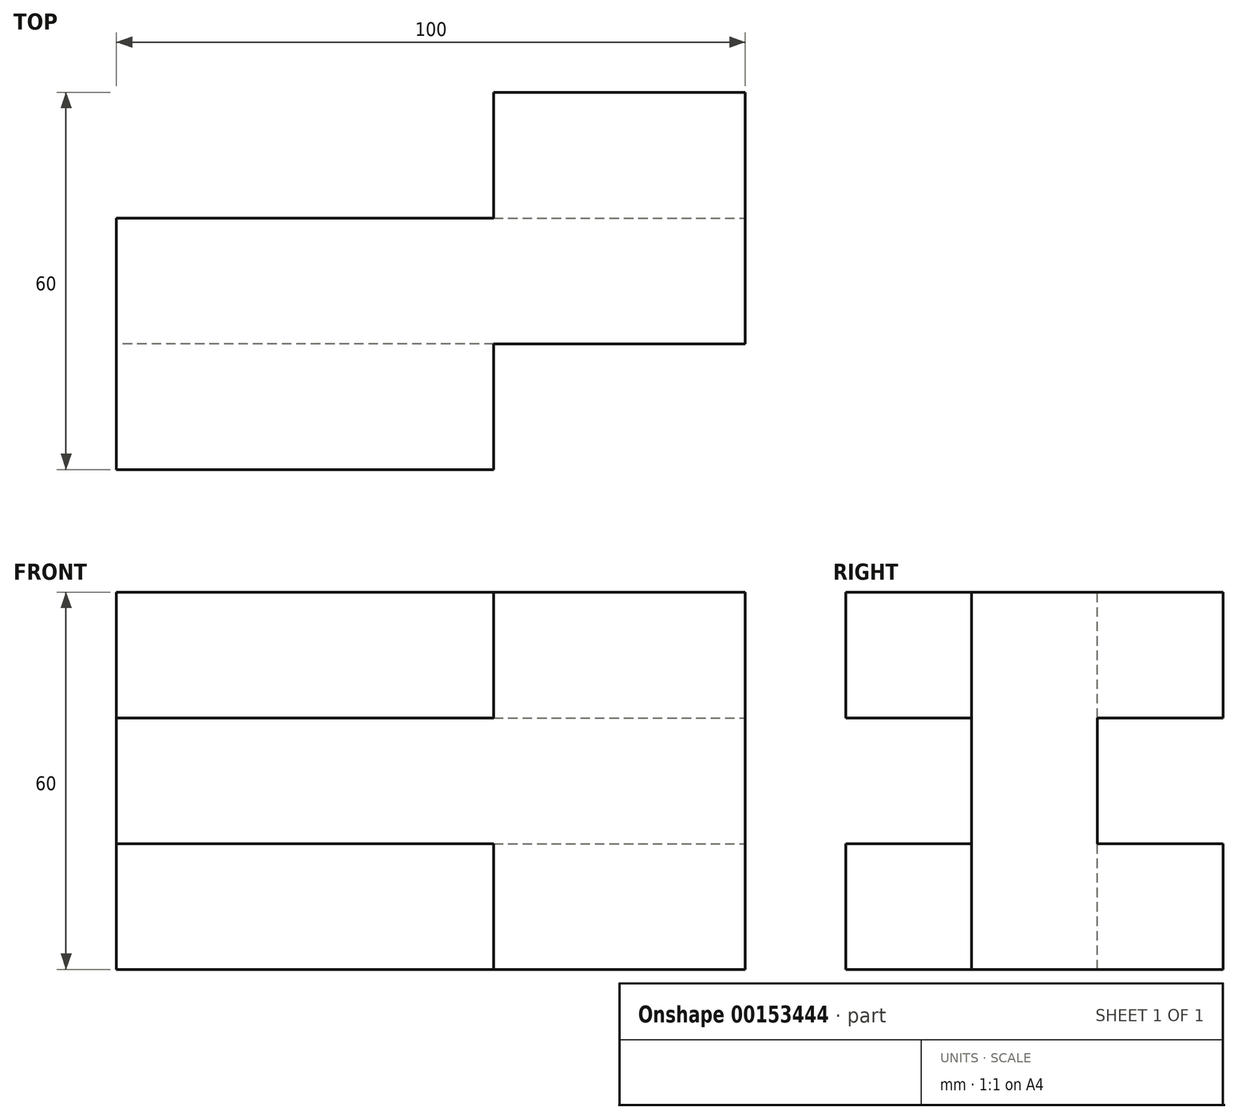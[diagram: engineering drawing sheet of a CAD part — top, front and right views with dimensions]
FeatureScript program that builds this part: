
annotation { "Feature Type Name" : "Feature", "Feature Type Description" : "" }
export const myFeature = defineFeature(function(context is Context, id is Id, definition is map)
    precondition{}
    {
        {
            var Q0;
            Q0=qCreatedBy(makeId("Top.planeOp"),FACE);
            var sketch = newSketch(context, id + "F0", { "sketchPlane" : qUnion([Q0])});
            skLineSegment(sketch, "E0.bottom", {"start": v(0, 0) * mm, "end": v(100, 0) * mm});
            skLineSegment(sketch, "E0.top", {"start": v(0, -60) * mm, "end": v(100, -60) * mm});
            skLineSegment(sketch, "E0.left", {"start": v(0, 0) * mm, "end": v(0, -60) * mm});
            skLineSegment(sketch, "E0.right", {"start": v(100, 0) * mm, "end": v(100, -60) * mm});
            skSolve(sketch);
        }
        {
            var Q0;
            Q0=makeQuery(id+"F0.imprint","IMPRINT",FACE,{"disambiguationData":[TD([[makeQuery(id+"F0.imprint","IMPRINT",EDGE,{"derivedFrom":sQuery(id+"F0.wireOp",EDGE,"E0.bottom")}),-1.0]])]});
            extrude(context, id + "F1", {"entities" : qUnion([Q0]), "depth" : 60 * mm});
        }
        {
            var Q0;
            Q0=makeQuery(id+"F1.opExtrude","CAP_FACE",FACE,{"disambiguationData":[OSD([sQuery(id+"F0.wireOp",EDGE,"E0.bottom"),sQuery(id+"F0.wireOp",EDGE,"E0.top"),sQuery(id+"F0.wireOp",EDGE,"E0.left"),sQuery(id+"F0.wireOp",EDGE,"E0.right")])],"isStart":true});
            var sketch = newSketch(context, id + "F2", { "sketchPlane" : qUnion([Q0])});
            skLineSegment(sketch, "E1.bottom", {"start": v(100, 60) * mm, "end": v(60, 60) * mm});
            skLineSegment(sketch, "E1.top", {"start": v(100, 40) * mm, "end": v(60, 40) * mm});
            skLineSegment(sketch, "E1.left", {"start": v(100, 60) * mm, "end": v(100, 40) * mm});
            skLineSegment(sketch, "E1.right", {"start": v(60, 60) * mm, "end": v(60, 40) * mm});
            skSolve(sketch);
        }
        {
            var Q0;
            Q0 = qSketchRegion(id + "F2", true);
            var Q1;
            Q1=sQuery(id+"F2.wireOp",EDGE,"E1.top");
            extrude(context, id + "F3", {"entities" : qUnion([Q0]), "operationType" : NewBodyOperationType.REMOVE, "surfaceEntities" : qUnion([Q1]), "endBound" : BoundingType.THROUGH_ALL, "oppositeDirection" : true, "depth" : 25 * mm});
        }
        {
            var Q0;
            Q0=makeQuery(id+"F1.opExtrude","SWEPT_FACE",FACE,{"disambiguationData":[OSD([sQuery(id+"F0.wireOp",EDGE,"E0.right")])]});
            var sketch = newSketch(context, id + "F4", { "sketchPlane" : qUnion([Q0])});
            skLineSegment(sketch, "E2.bottom", {"start": v(0, 40) * mm, "end": v(-20, 40) * mm});
            skLineSegment(sketch, "E2.top", {"start": v(0, 20) * mm, "end": v(-20, 20) * mm});
            skLineSegment(sketch, "E2.left", {"start": v(0, 40) * mm, "end": v(0, 20) * mm});
            skLineSegment(sketch, "E2.right", {"start": v(-20, 40) * mm, "end": v(-20, 20) * mm});
            skSolve(sketch);
        }
        {
            var Q0;
            Q0 = qSketchRegion(id + "F4", true);
            var Q1;
            Q1=sQuery(id+"F4.wireOp",EDGE,"E2.right");
            var Q2;
            Q2=sQuery(id+"F4.wireOp",EDGE,"E2.top");
            var Q3;
            Q3=sQuery(id+"F4.wireOp",EDGE,"E2.left");
            var Q4;
            Q4=sQuery(id+"F4.wireOp",EDGE,"E2.bottom");
            extrude(context, id + "F5", {"entities" : qUnion([Q0]), "operationType" : NewBodyOperationType.REMOVE, "surfaceEntities" : qUnion([Q1, Q2, Q3, Q4]), "endBound" : BoundingType.THROUGH_ALL, "oppositeDirection" : true, "depth" : 25 * mm});
        }
        {
            var Q0;
            Q0=makeQuery(id+"F1.opExtrude","CAP_FACE",FACE,{"disambiguationData":[OSD([sQuery(id+"F0.wireOp",EDGE,"E0.bottom"),sQuery(id+"F0.wireOp",EDGE,"E0.top"),sQuery(id+"F0.wireOp",EDGE,"E0.left"),sQuery(id+"F0.wireOp",EDGE,"E0.right")])],"isStart":false});
            var sketch = newSketch(context, id + "F6", { "sketchPlane" : qUnion([Q0])});
            skLineSegment(sketch, "E3.bottom", {"start": v(0, 0) * mm, "end": v(60, 0) * mm});
            skLineSegment(sketch, "E3.top", {"start": v(0, -20) * mm, "end": v(60, -20) * mm});
            skLineSegment(sketch, "E3.left", {"start": v(0, 0) * mm, "end": v(0, -20) * mm});
            skLineSegment(sketch, "E3.right", {"start": v(60, 0) * mm, "end": v(60, -20) * mm});
            skSolve(sketch);
        }
        {
            var Q0;
            Q0 = qSketchRegion(id + "F6", true);
            extrude(context, id + "F7", {"entities" : qUnion([Q0]), "operationType" : NewBodyOperationType.REMOVE, "endBound" : BoundingType.THROUGH_ALL, "oppositeDirection" : true, "depth" : 25 * mm});
        }
        {
            var Q0;
            Q0=makeQuery(id+"F1.opExtrude","SWEPT_FACE",FACE,{"disambiguationData":[OSD([sQuery(id+"F0.wireOp",EDGE,"E0.left")])]});
            var sketch = newSketch(context, id + "F8", { "sketchPlane" : qUnion([Q0])});
            skLineSegment(sketch, "E4.bottom", {"start": v(60, 20) * mm, "end": v(40, 20) * mm});
            skLineSegment(sketch, "E4.top", {"start": v(60, 40) * mm, "end": v(40, 40) * mm});
            skLineSegment(sketch, "E4.left", {"start": v(60, 20) * mm, "end": v(60, 40) * mm});
            skLineSegment(sketch, "E4.right", {"start": v(40, 20) * mm, "end": v(40, 40) * mm});
            skSolve(sketch);
        }
        {
            var Q0;
            Q0 = qSketchRegion(id + "F8", true);
            extrude(context, id + "F9", {"entities" : qUnion([Q0]), "operationType" : NewBodyOperationType.REMOVE, "endBound" : BoundingType.THROUGH_ALL, "oppositeDirection" : true, "depth" : 25 * mm});
        }
    });
